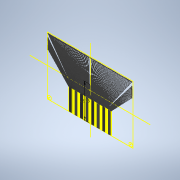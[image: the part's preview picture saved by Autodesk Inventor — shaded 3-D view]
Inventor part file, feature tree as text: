
AUTODESK INVENTOR PART (.ipt)
format: ipt  version: 2021 (Build 250183000, 183)  size: 3,749,376 bytes
history: native  units: in
note: dims shown in document units (in); Inventor stores cm internally (conversion verified against a paired STEP export)
features: sketch x13, extrude x10, projected_geometry x9, pattern_linear x7, mirror x5, hole x1
ambient origin geometry x8: Origin, YZ Plane, XZ Plane, XY Plane, X Axis, Y Axis, Z Axis, Center Point
bodies: Solid1 (feature_tree)
feature tree (45):
  extrude  "Extrusion1"  Depth=2.7in
  hole  "Hole1"  [1 undecoded]
  mirror  "Mirror3"
  sketch  "Sketch9"  dims[d42=0.1in d43=0.11in]
  extrude  "Extrusion5"  Depth=0.11in
  pattern_linear  "Rectangular Pattern6"  Count1=101 Spacing1=0.039in
  extrude  "Extrusion6"  Depth=0.032in TaperAngle=0.0deg
  pattern_linear  "Rectangular Pattern7"  Count1=101 Spacing1=0.039in
  extrude  "Extrusion7"  TaperAngle=0.0deg  [1 undecoded]
  mirror  "Mirror4"
  extrude  "Extrusion9"  Depth=2.0in
  pattern_linear  "Rectangular Pattern9"  Spacing1=0.008in  [1 undecoded]
  sketch  "Sketch16"  dims[d54=1.75in]
  pattern_linear  "Rectangular Pattern10"  Spacing1=1.0in  [1 undecoded]
  extrude  "Extrusion10"  Depth=0.004in TaperAngle=0.0deg
  pattern_linear  "Rectangular Pattern11"  Count1=125 Spacing1=0.016in
  mirror  "Mirror5"
  extrude  "Extrusion11"  Depth=1.0in
  mirror  "Mirror6"
  extrude  "Extrusion12"  Depth=1.0in
  pattern_linear  "Rectangular Pattern12"  Spacing1=0.05in  [1 undecoded]
  extrude  "Extrusion13"  Depth=1.0in
  pattern_linear  "Rectangular Pattern13"  Spacing1=0.0in  [1 undecoded]
  mirror  "Mirror7"
  extrude  "Extrusion14"  Depth=1.0in
  sketch  "Sketch1"  dims[d0=4.0in d1=2.7in]
  sketch  "Sketch7"  dims[d2=0.04in d3=0.0in d41=0.1719in]
  projected_geometry  "Projected Loop6"
  projected_geometry  "Projected Loop8"
  sketch  "Sketch11"  dims[d44=0.17in d45=0.75in d46=0.313in d47=0.164in d48=0.5635in d49=0.12in]
  projected_geometry  "Projected Loop9"
  sketch  "Sketch12"  dims[d50=0.8108in]
  sketch  "Sketch13"  dims[d52=1.5748in]
  sketch  "Sketch15"  dims[d53=0.02in]
  projected_geometry  "Projected Loop11"
  projected_geometry  "Projected Loop12"
  sketch  "Sketch17"  dims[d55=0.0in d56=0.0in d57=39.7638in d59=0.039in]
  projected_geometry  "Projected Loop13"
  sketch  "Sketch18"  dims[d60=0.032in d61=0.0014in d62=0.0in d63=39.7638in d65=0.039in]
  projected_geometry  "Projected Loop14"
  sketch  "Sketch19"  dims[d66=0.0197in d69=0.0in d70=0.0in]
  projected_geometry  "Projected Loop15"
  sketch  "Sketch20"  dims[d71=2.65in d82=2.0in]
  sketch  "Sketch21"  dims[d83=0.25in d84=0.008in d86=1.0in d87=0.004in d88=0.0in d89=49.2126in d91=0.016in d92=39.7638in d94=0.039in d95=0.0198in d96=0.05in d97=0.175in d98=0.0in d99=0.0in d100=5.1181in d102=0.039in d103=0.008in d104=0.008in d105=0.008in d106=0.008in d107=0.008in d108=0.008in d109=0.008in d110=0.008in d111=0.008in d112=0.008in d113=0.008in d114=0.008in d115=0.008in d116=0.008in d117=0.008in d118=0.008in d119=0.008in d120=0.008in d121=0.008in d122=0.008in d123=0.008in d124=0.008in d125=0.008in d126=0.008in d127=0.008in d128=0.008in d129=0.008in d130=0.008in d131=0.008in d132=0.008in d133=0.008in d134=0.008in d135=0.008in d136=0.008in d137=0.008in d138=0.008in d139=0.008in d140=0.008in d141=0.008in d142=0.008in d143=0.008in d144=0.008in d145=0.008in d146=0.008in d147=0.008in d148=0.008in d149=0.008in d150=0.008in d151=0.008in d152=0.008in d153=0.008in d154=0.008in d155=0.008in d156=0.008in d157=0.008in d158=0.008in d159=0.008in d160=0.008in d161=0.008in d162=0.008in d163=0.008in d164=0.008in d165=0.008in d166=0.004in d167=0.0in d168=0.008in d169=0.03in d170=0.004in d171=0.0in d172=5.1181in d174=0.039in d175=0.032in d176=0.004in d177=0.0in d178=39.7638in d180=0.039in d181=1.0in d182=0.0in]
  projected_geometry  "Projected Loop16"
note: 6 required parameter values undecoded (feature->parameter linkage not recoverable at this tier; creation-order binding heuristic only, values carry confidence <= 0.55)
